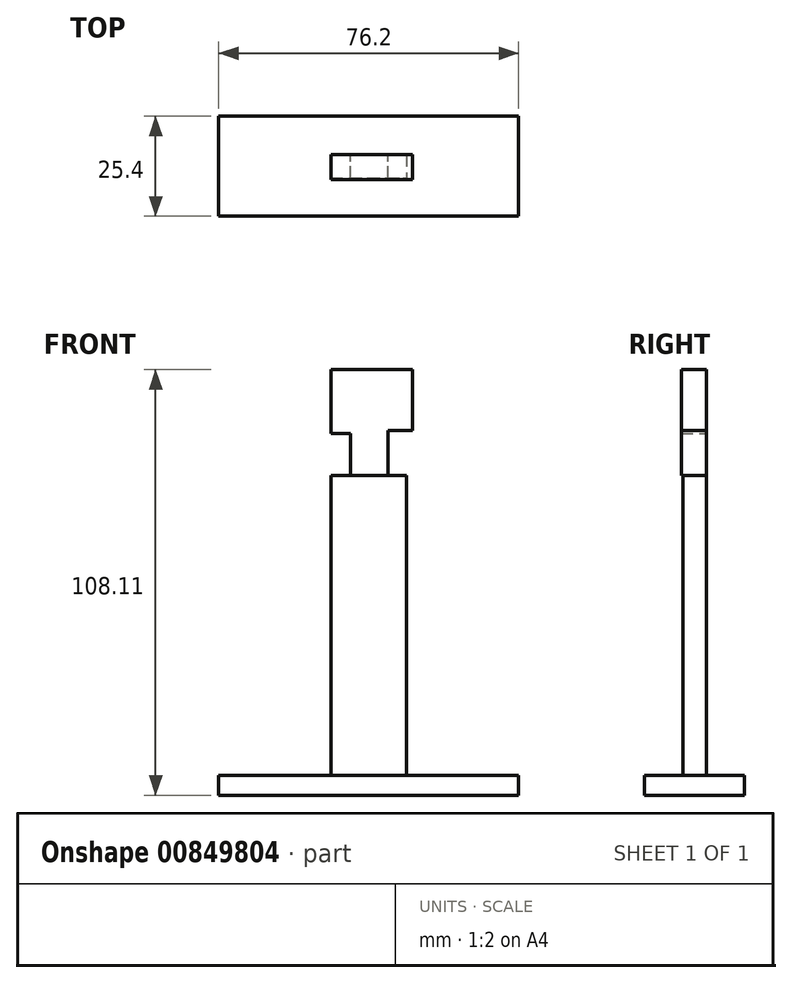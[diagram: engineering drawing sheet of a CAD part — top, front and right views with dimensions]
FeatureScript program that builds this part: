
annotation { "Feature Type Name" : "Feature", "Feature Type Description" : "" }
export const myFeature = defineFeature(function(context is Context, id is Id, definition is map)
    precondition{}
    {
        {
            var Q0;
            Q0=qCreatedBy(makeId("Top.planeOp"),FACE);
            var sketch = newSketch(context, id + "F0", { "sketchPlane" : qUnion([Q0])});
            skLineSegment(sketch, "E0.bottom", {"start": v(-38.1, 12.7) * mm, "end": v(38.1, 12.7) * mm});
            skLineSegment(sketch, "E0.top", {"start": v(-38.1, -12.7) * mm, "end": v(38.1, -12.7) * mm});
            skLineSegment(sketch, "E0.left", {"start": v(-38.1, 12.7) * mm, "end": v(-38.1, -12.7) * mm});
            skLineSegment(sketch, "E0.right", {"start": v(38.1, 12.7) * mm, "end": v(38.1, -12.7) * mm});
            skPoint(sketch, "E0.middle", {"position": v(0, 0) * mm});
            skSolve(sketch);
        }
        {
            var Q0;
            Q0=makeQuery(id+"F0.imprint","IMPRINT",FACE,{"disambiguationData":[TD([[makeQuery(id+"F0.imprint","IMPRINT",EDGE,{"derivedFrom":sQuery(id+"F0.wireOp",EDGE,"E0.bottom")}),-1.0]])]});
            extrude(context, id + "F1", {"entities" : qUnion([Q0]), "depth" : 5.08 * mm, "offsetDistance" : 25.4 * mm});
        }
        {
            var Q0;
            Q0=makeQuery(id+"F1.opExtrude","CAP_FACE",FACE,{"disambiguationData":[OSD([sQuery(id+"F0.wireOp",EDGE,"E0.bottom"),sQuery(id+"F0.wireOp",EDGE,"E0.top"),sQuery(id+"F0.wireOp",EDGE,"E0.left"),sQuery(id+"F0.wireOp",EDGE,"E0.right")])],"isStart":false});
            var sketch = newSketch(context, id + "F2", { "sketchPlane" : qUnion([Q0])});
            skLineSegment(sketch, "E1.bottom", {"start": v(-9.64, 2.97) * mm, "end": v(9.64, 2.97) * mm});
            skLineSegment(sketch, "E1.top", {"start": v(-9.64, -2.97) * mm, "end": v(9.64, -2.97) * mm});
            skLineSegment(sketch, "E1.left", {"start": v(-9.64, 2.97) * mm, "end": v(-9.64, -2.97) * mm});
            skLineSegment(sketch, "E1.right", {"start": v(9.64, 2.97) * mm, "end": v(9.64, -2.97) * mm});
            skPoint(sketch, "E1.middle", {"position": v(0, 0) * mm});
            skSolve(sketch);
        }
        {
            var Q0;
            Q0 = qSketchRegion(id + "F2", true);
            extrude(context, id + "F3", {"entities" : qUnion([Q0]), "operationType" : NewBodyOperationType.ADD, "depth" : 76.2 * mm, "offsetDistance" : 25.4 * mm});
        }
        {
            var Q0;
            Q0=makeQuery(id+"F3.opExtrude","SWEPT_FACE",FACE,{"disambiguationData":[OSD([sQuery(id+"F2.wireOp",EDGE,"E1.bottom")])]});
            var sketch = newSketch(context, id + "F4", { "sketchPlane" : qUnion([Q0])});
            skLineSegment(sketch, "E2", {"start": v(4.68, 81.28) * mm, "end": v(4.68, 91.88) * mm});
            skLineSegment(sketch, "E3", {"start": v(4.68, 91.88) * mm, "end": v(9.64, 91.88) * mm});
            skLineSegment(sketch, "E4", {"start": v(9.64, 91.88) * mm, "end": v(9.64, 108.11) * mm});
            skLineSegment(sketch, "E5", {"start": v(9.64, 108.11) * mm, "end": v(-11.08, 108.11) * mm});
            skLineSegment(sketch, "E6", {"start": v(-11.08, 108.11) * mm, "end": v(-11.08, 92.66) * mm});
            skLineSegment(sketch, "E7", {"start": v(-11.08, 92.66) * mm, "end": v(-4.84, 92.66) * mm});
            skLineSegment(sketch, "E8", {"start": v(-4.84, 92.66) * mm, "end": v(-4.84, 81.28) * mm});
            skLineSegment(sketch, "E9", {"start": v(4.68, 81.28) * mm, "end": v(-4.84, 81.28) * mm});
            skSolve(sketch);
        }
        {
            var Q0;
            Q0=makeQuery(id+"F4.imprint","IMPRINT",FACE,{"disambiguationData":[TD([[makeQuery(id+"F4.imprint","IMPRINT",EDGE,{"derivedFrom":sQuery(id+"F4.wireOp",EDGE,"E2")}),1.0]])]});
            extrude(context, id + "F5", {"entities" : qUnion([Q0]), "operationType" : NewBodyOperationType.ADD, "oppositeDirection" : true, "depth" : 6.35 * mm, "offsetDistance" : 25.4 * mm});
        }
    });
